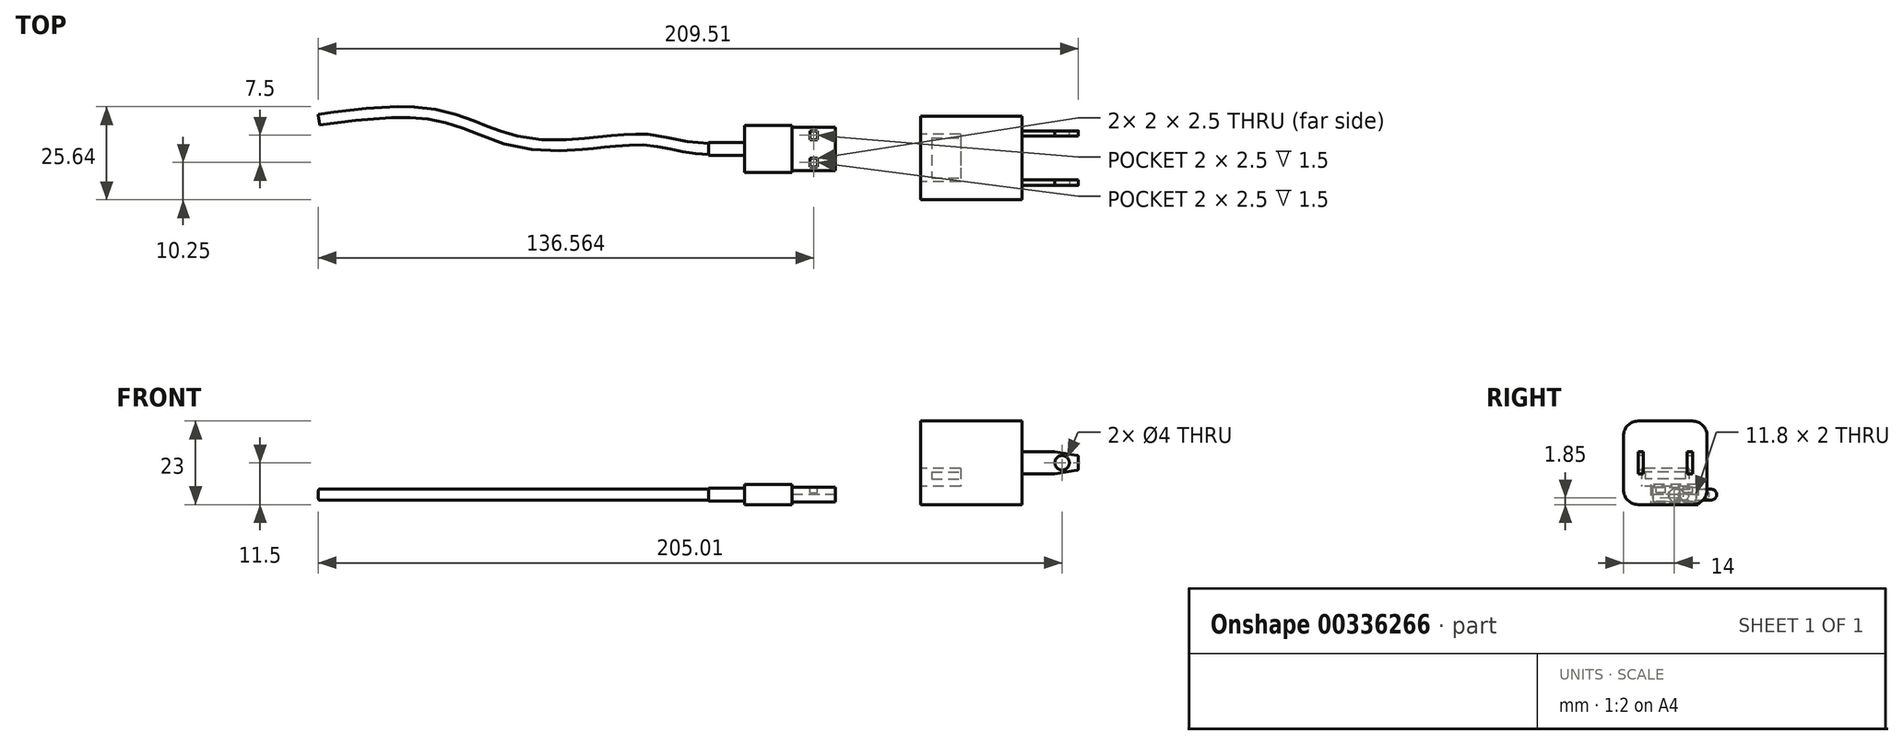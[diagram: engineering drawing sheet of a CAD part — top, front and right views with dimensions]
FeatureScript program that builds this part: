
annotation { "Feature Type Name" : "Feature", "Feature Type Description" : "" }
export const myFeature = defineFeature(function(context is Context, id is Id, definition is map)
    precondition{}
    {
        {
            var Q0;
            Q0=qCreatedBy(makeId("Top.planeOp"),FACE);
            var sketch = newSketch(context, id + "F0", { "sketchPlane" : qUnion([Q0])});
            skLineSegment(sketch, "E0.bottom", {"start": v(-14, 11.5) * mm, "end": v(14, 11.5) * mm});
            skLineSegment(sketch, "E0.top", {"start": v(-14, -11.5) * mm, "end": v(14, -11.5) * mm});
            skLineSegment(sketch, "E0.left", {"start": v(-14, 11.5) * mm, "end": v(-14, -11.5) * mm});
            skLineSegment(sketch, "E0.right", {"start": v(14, 11.5) * mm, "end": v(14, -11.5) * mm});
            skLineSegment(sketch, "E1", {"start": v(0, -11.5) * mm, "end": v(0, 0) * mm});
            skLineSegment(sketch, "E2", {"start": v(0, 0) * mm, "end": v(0, 11.5) * mm});
            skLineSegment(sketch, "E3", {"start": v(14, 0) * mm, "end": v(0, 0) * mm});
            skLineSegment(sketch, "E4", {"start": v(0, 0) * mm, "end": v(-14, 0) * mm});
            skLineSegment(sketch, "E5.bottom", {"start": v(-49.45, 8.5) * mm, "end": v(-37.45, 8.5) * mm});
            skLineSegment(sketch, "E5.top", {"start": v(-49.45, -3.5) * mm, "end": v(-37.45, -3.5) * mm});
            skLineSegment(sketch, "E5.left", {"start": v(-49.45, 8.5) * mm, "end": v(-49.45, -3.5) * mm});
            skLineSegment(sketch, "E5.right", {"start": v(-37.45, 8.5) * mm, "end": v(-37.45, -3.5) * mm});
            skLineSegment(sketch, "E6.bottom", {"start": v(-62.45, 9) * mm, "end": v(-49.45, 9) * mm});
            skLineSegment(sketch, "E6.top", {"start": v(-62.45, -4) * mm, "end": v(-49.45, -4) * mm});
            skLineSegment(sketch, "E6.left", {"start": v(-62.45, 9) * mm, "end": v(-62.45, -4) * mm});
            skLineSegment(sketch, "E6.right", {"start": v(-49.45, 9) * mm, "end": v(-49.45, -4) * mm});
            skPoint(sketch, "E7.endSnap0", {"position": v(-49.45, 2.5) * mm});
            skLineSegment(sketch, "E8.bottom", {"start": v(-44.45, 7.5) * mm, "end": v(-42.45, 7.5) * mm});
            skLineSegment(sketch, "E8.top", {"start": v(-44.45, 5) * mm, "end": v(-42.45, 5) * mm});
            skLineSegment(sketch, "E8.left", {"start": v(-44.45, 7.5) * mm, "end": v(-44.45, 5) * mm});
            skLineSegment(sketch, "E8.right", {"start": v(-42.45, 7.5) * mm, "end": v(-42.45, 5) * mm});
            skLineSegment(sketch, "E9.bottom", {"start": v(-44.45, 0) * mm, "end": v(-42.45, 0) * mm});
            skLineSegment(sketch, "E9.top", {"start": v(-44.45, -2.5) * mm, "end": v(-42.45, -2.5) * mm});
            skLineSegment(sketch, "E9.left", {"start": v(-44.45, 0) * mm, "end": v(-44.45, -2.5) * mm});
            skLineSegment(sketch, "E9.right", {"start": v(-42.45, 0) * mm, "end": v(-42.45, -2.5) * mm});
            skLineSegment(sketch, "E10", {"start": v(-44.45, 6.25) * mm, "end": v(-49.45, 6.25) * mm});
            skLineSegment(sketch, "E11", {"start": v(-44.45, -1.25) * mm, "end": v(-49.45, -1.25) * mm});
            skLineSegment(sketch, "E12", {"start": v(-42.45, 6.25) * mm, "end": v(-37.45, 6.25) * mm});
            skLineSegment(sketch, "E13", {"start": v(-42.45, -1.25) * mm, "end": v(-37.45, -1.25) * mm});
            skLineSegment(sketch, "E14", {"start": v(-43.45, 7.5) * mm, "end": v(-43.45, 8.5) * mm});
            skLineSegment(sketch, "E15", {"start": v(-43.45, -3.5) * mm, "end": v(-43.45, -2.5) * mm});
            skSolve(sketch);
        }
        {
            var Q0;
            {var subQ3=sQuery(id+"F0.wireOp",EDGE,"E1");Q0=makeQuery(id+"F0.imprint","IMPRINT",FACE,{"disambiguationData":[TD([[makeQuery(id+"F0.imprint","IMPRINT",EDGE,{"derivedFrom":subQ3}),-1.0]])]});}
            var Q1;
            {var subQ3=sQuery(id+"F0.wireOp",EDGE,"E2");Q1=makeQuery(id+"F0.imprint","IMPRINT",FACE,{"disambiguationData":[TD([[makeQuery(id+"F0.imprint","IMPRINT",EDGE,{"derivedFrom":subQ3}),-1.0]])]});}
            var Q2;
            {var subQ3=sQuery(id+"F0.wireOp",EDGE,"E2");Q2=makeQuery(id+"F0.imprint","IMPRINT",FACE,{"disambiguationData":[TD([[makeQuery(id+"F0.imprint","IMPRINT",EDGE,{"derivedFrom":subQ3}),1.0]])]});}
            var Q3;
            {var subQ3=sQuery(id+"F0.wireOp",EDGE,"E1");Q3=makeQuery(id+"F0.imprint","IMPRINT",FACE,{"disambiguationData":[TD([[makeQuery(id+"F0.imprint","IMPRINT",EDGE,{"derivedFrom":subQ3}),1.0]])]});}
            extrude(context, id + "F1", {"entities" : qUnion([Q0, Q1, Q2, Q3]), "depth" : 23 * mm});
        }
        {
            var Q0;
            Q0=makeQuery(id+"F1.opExtrude","SWEPT_FACE",FACE,{"disambiguationData":[OSD([sQuery(id+"F0.wireOp",EDGE,"E0.left")])]});
            var sketch = newSketch(context, id + "F2", { "sketchPlane" : qUnion([Q0])});
            skLineSegment(sketch, "E16.bottom", {"start": v(-6.5, 10) * mm, "end": v(6.5, 10) * mm});
            skLineSegment(sketch, "E16.top", {"start": v(-6.5, 5) * mm, "end": v(6.5, 5) * mm});
            skLineSegment(sketch, "E16.left", {"start": v(-6.5, 10) * mm, "end": v(-6.5, 5) * mm});
            skLineSegment(sketch, "E16.right", {"start": v(6.5, 10) * mm, "end": v(6.5, 5) * mm});
            skSolve(sketch);
        }
        {
            var Q0;
            Q0=makeQuery(id+"F1.opExtrude","CAP_EDGE",EDGE,{"disambiguationData":[OSD([sQuery(id+"F0.wireOp",EDGE,"E0.bottom")])],"isStart":false});
            var Q1;
            Q1=makeQuery(id+"F1.opExtrude","CAP_EDGE",EDGE,{"disambiguationData":[OSD([sQuery(id+"F0.wireOp",EDGE,"E0.top")])],"isStart":false});
            var Q2;
            Q2=makeQuery(id+"F1.opExtrude","CAP_EDGE",EDGE,{"disambiguationData":[OSD([sQuery(id+"F0.wireOp",EDGE,"E0.top")])],"isStart":true});
            var Q3;
            Q3=makeQuery(id+"F1.opExtrude","CAP_EDGE",EDGE,{"disambiguationData":[OSD([sQuery(id+"F0.wireOp",EDGE,"E0.bottom")])],"isStart":true});
            fillet(context, id + "F3", {"entities" : qUnion([Q0, Q1, Q2, Q3]), "radius" : 4 * mm, "tangentPropagation" : true, "allowEdgeOverflow" : false});
        }
        {
            var Q0;
            Q0=makeQuery(id+"F1.opExtrude","SWEPT_FACE",FACE,{"disambiguationData":[OSD([sQuery(id+"F0.wireOp",EDGE,"E0.right")])]});
            var sketch = newSketch(context, id + "F4", { "sketchPlane" : qUnion([Q0])});
            skLineSegment(sketch, "E17.bottom", {"start": v(-7.5, 14.5) * mm, "end": v(-6, 14.5) * mm});
            skLineSegment(sketch, "E17.top", {"start": v(-7.5, 8.5) * mm, "end": v(-6, 8.5) * mm});
            skLineSegment(sketch, "E17.left", {"start": v(-7.5, 14.5) * mm, "end": v(-7.5, 8.5) * mm});
            skLineSegment(sketch, "E17.right", {"start": v(-6, 14.5) * mm, "end": v(-6, 8.5) * mm});
            skLineSegment(sketch, "E18.bottom", {"start": v(6, 14.5) * mm, "end": v(7.5, 14.5) * mm});
            skLineSegment(sketch, "E18.top", {"start": v(6, 8.5) * mm, "end": v(7.5, 8.5) * mm});
            skLineSegment(sketch, "E18.left", {"start": v(6, 14.5) * mm, "end": v(6, 8.5) * mm});
            skLineSegment(sketch, "E18.right", {"start": v(7.5, 14.5) * mm, "end": v(7.5, 8.5) * mm});
            skLineSegment(sketch, "E19", {"start": v(-6.75, 14.5) * mm, "end": v(-6.75, 23) * mm});
            skLineSegment(sketch, "E20", {"start": v(-6.75, 8.5) * mm, "end": v(-6.75, 0) * mm});
            skLineSegment(sketch, "E21", {"start": v(6.75, 8.5) * mm, "end": v(6.75, 0) * mm});
            skLineSegment(sketch, "E22", {"start": v(6.75, 14.5) * mm, "end": v(6.75, 23) * mm});
            skLineSegment(sketch, "E23", {"start": v(-7.5, 11.5) * mm, "end": v(-11.5, 11.5) * mm});
            skLineSegment(sketch, "E24", {"start": v(7.5, 11.5) * mm, "end": v(11.5, 11.5) * mm});
            skSolve(sketch);
        }
        {
            var Q0;
            {var subQ0=sQuery(id+"F4.wireOp",EDGE,"E17.right");Q0=makeQuery(id+"F4.imprint","IMPRINT",FACE,{"disambiguationData":[TD([[makeQuery(id+"F4.imprint","IMPRINT",EDGE,{"derivedFrom":subQ0}),-1.0]])]});}
            var Q1;
            {var subQ4=sQuery(id+"F4.wireOp",EDGE,"E18.left");Q1=makeQuery(id+"F4.imprint","IMPRINT",FACE,{"disambiguationData":[TD([[makeQuery(id+"F4.imprint","IMPRINT",EDGE,{"derivedFrom":subQ4}),1.0]])]});}
            extrude(context, id + "F5", {"entities" : qUnion([Q0, Q1]), "depth" : 9 * mm});
        }
        {
            var Q0;
            Q0=makeQuery(id+"F5.opExtrude","SWEPT_FACE",FACE,{"disambiguationData":[OSD([sQuery(id+"F4.wireOp",EDGE,"E17.left")])]});
            var sketch = newSketch(context, id + "F6", { "sketchPlane" : qUnion([Q0])});
            skLineSegment(sketch, "E25", {"start": v(29.5, 13.5) * mm, "end": v(29.5, 9.5) * mm});
            skCircle(sketch, "E26", {"center": v(25, 11.5) * mm, "radius": 2 * mm});
            skPoint(sketch, "E27.endSnap0", {"position": v(23, 11.5) * mm});
            skLineSegment(sketch, "E28", {"start": v(23, 14.5) * mm, "end": v(29.5, 13.5) * mm});
            skLineSegment(sketch, "E29", {"start": v(29.5, 9.5) * mm, "end": v(23, 8.5) * mm});
            skSolve(sketch);
        }
        {
            var Q0;
            Q0=makeQuery(id+"F6.imprint","IMPRINT",FACE,{"disambiguationData":[TD([[makeQuery(id+"F6.imprint","IMPRINT",EDGE,{"derivedFrom":sQuery(id+"F6.wireOp",EDGE,"E25")}),-1.0]])]});
            var Q1;
            Q1=makeQuery(id+"F6.imprint","IMPRINT",FACE,{"disambiguationData":[TD([[makeQuery(id+"F6.imprint","IMPRINT",EDGE,{"derivedFrom":sQuery(id+"F6.wireOp",EDGE,"E26")}),1.0]])]});
            extrude(context, id + "F7", {"entities" : qUnion([Q0, Q1]), "operationType" : NewBodyOperationType.ADD, "oppositeDirection" : true, "depth" : 1.5 * mm});
        }
        {
            var Q0;
            Q0=makeQuery(id+"F6.imprint","IMPRINT",FACE,{"disambiguationData":[TD([[makeQuery(id+"F6.imprint","IMPRINT",EDGE,{"derivedFrom":sQuery(id+"F6.wireOp",EDGE,"E26")}),1.0]])]});
            extrude(context, id + "F8", {"entities" : qUnion([Q0]), "operationType" : NewBodyOperationType.REMOVE, "oppositeDirection" : true, "depth" : 1.5 * mm});
        }
        {
            var Q0;
            Q0=makeQuery(id+"F5.opExtrude","SWEPT_BODY",BODY,{"disambiguationData":[OSD([sQuery(id+"F4.wireOp",EDGE,"E17.bottom"),sQuery(id+"F4.wireOp",EDGE,"E17.top"),sQuery(id+"F4.wireOp",EDGE,"E17.left"),sQuery(id+"F4.wireOp",EDGE,"E17.right")])]});
            var Q1;
            Q1=qCreatedBy(makeId("Front.planeOp"),FACE);
            mirror(context, id + "F9", {"entities" : qUnion([Q0]), "mirrorPlane" : qUnion([Q1])});
        }
        {
            var Q0;
            Q0=makeQuery(id+"F5.opExtrude","SWEPT_BODY",BODY,{"disambiguationData":[OSD([sQuery(id+"F4.wireOp",EDGE,"E18.bottom"),sQuery(id+"F4.wireOp",EDGE,"E18.top"),sQuery(id+"F4.wireOp",EDGE,"E18.left"),sQuery(id+"F4.wireOp",EDGE,"E18.right")])]});
            deleteBodies(context, id + "F10", {"entities" : qUnion([Q0])});
        }
        {
            var Q0;
            Q0=makeQuery(id+"F7.opExtrude","SWEPT_EDGE",EDGE,{"disambiguationData":[OSD([sQuery(id+"F6.wireOp",EDGE,"E25"),sQuery(id+"F6.wireOp",EDGE,"E28")])]});
            var Q1;
            Q1=makeQuery(id+"F7.opExtrude","SWEPT_EDGE",EDGE,{"disambiguationData":[OSD([sQuery(id+"F6.wireOp",EDGE,"E25"),sQuery(id+"F6.wireOp",EDGE,"E29")])]});
            var Q2;
            Q2=makeQuery(id+"F9.opPattern","COPY",EDGE,{"derivedFrom":makeQuery(id+"F7.opExtrude","SWEPT_EDGE",EDGE,{"disambiguationData":[OSD([sQuery(id+"F6.wireOp",EDGE,"E25"),sQuery(id+"F6.wireOp",EDGE,"E28")])]}),"instanceName":"1"});
            var Q3;
            Q3=makeQuery(id+"F9.opPattern","COPY",EDGE,{"derivedFrom":makeQuery(id+"F7.opExtrude","SWEPT_EDGE",EDGE,{"disambiguationData":[OSD([sQuery(id+"F6.wireOp",EDGE,"E25"),sQuery(id+"F6.wireOp",EDGE,"E29")])]}),"instanceName":"1"});
            fillet(context, id + "F11", {"entities" : qUnion([Q0, Q1, Q2, Q3]), "radius" : 0.5 * mm, "tangentPropagation" : true, "allowEdgeOverflow" : false});
        }
        {
            var Q0;
            Q0=makeQuery(id+"F2.imprint","IMPRINT",FACE,{"disambiguationData":[TD([[makeQuery(id+"F2.imprint","IMPRINT",EDGE,{"derivedFrom":sQuery(id+"F2.wireOp",EDGE,"E16.bottom")}),-1.0]])]});
            extrude(context, id + "F12", {"entities" : qUnion([Q0]), "operationType" : NewBodyOperationType.REMOVE, "oppositeDirection" : true, "depth" : 11 * mm});
        }
        {
            var Q0;
            Q0=makeQuery(id+"F12.boolean.opBoolean","COPY",FACE,{"derivedFrom":makeQuery(id+"F12.opExtrude","CAP_FACE",FACE,{"disambiguationData":[OSD([sQuery(id+"F2.wireOp",EDGE,"E16.bottom"),sQuery(id+"F2.wireOp",EDGE,"E16.top"),sQuery(id+"F2.wireOp",EDGE,"E16.left"),sQuery(id+"F2.wireOp",EDGE,"E16.right")])],"isStart":false})});
            var sketch = newSketch(context, id + "F13", { "sketchPlane" : qUnion([Q0])});
            skLineSegment(sketch, "E30.bottom", {"start": v(-5.5, 9) * mm, "end": v(5.5, 9) * mm});
            skLineSegment(sketch, "E30.top", {"start": v(-5.5, 7) * mm, "end": v(5.5, 7) * mm});
            skLineSegment(sketch, "E30.left", {"start": v(-5.5, 9) * mm, "end": v(-5.5, 7) * mm});
            skLineSegment(sketch, "E30.right", {"start": v(5.5, 9) * mm, "end": v(5.5, 7) * mm});
            skSolve(sketch);
        }
        {
            var Q0;
            Q0=makeQuery(id+"F13.imprint","IMPRINT",FACE,{"disambiguationData":[TD([[makeQuery(id+"F13.imprint","IMPRINT",EDGE,{"derivedFrom":sQuery(id+"F13.wireOp",EDGE,"E30.bottom")}),-1.0]])]});
            extrude(context, id + "F14", {"entities" : qUnion([Q0]), "depth" : 8 * mm});
        }
        {
            var Q0;
            {var subQ2=sQuery(id+"F0.wireOp",EDGE,"E6.bottom");Q0=makeQuery(id+"F0.imprint","IMPRINT",FACE,{"disambiguationData":[TD([[makeQuery(id+"F0.imprint","IMPRINT",EDGE,{"derivedFrom":subQ2}),-1.0]])]});}
            extrude(context, id + "F15", {"entities" : qUnion([Q0]), "depth" : 5.5 * mm});
        }
        {
            var Q0;
            Q0=makeQuery(id+"F15.opExtrude","SWEPT_FACE",FACE,{"disambiguationData":[OSD([sQuery(id+"F0.wireOp",EDGE,"E6.right")])]});
            var sketch = newSketch(context, id + "F16", { "sketchPlane" : qUnion([Q0])});
            skLineSegment(sketch, "E31.bottom", {"start": v(-3.5, 4.75) * mm, "end": v(8.5, 4.75) * mm});
            skLineSegment(sketch, "E31.top", {"start": v(-3.5, 0.75) * mm, "end": v(8.5, 0.75) * mm});
            skLineSegment(sketch, "E31.left", {"start": v(-3.5, 4.75) * mm, "end": v(-3.5, 0.75) * mm});
            skLineSegment(sketch, "E31.right", {"start": v(8.5, 4.75) * mm, "end": v(8.5, 0.75) * mm});
            skLineSegment(sketch, "E32", {"start": v(-3.5, 2.75) * mm, "end": v(-4, 2.75) * mm});
            skPoint(sketch, "E32.endSnap0", {"position": v(-4, 2.75) * mm});
            skLineSegment(sketch, "E33", {"start": v(2.5, 4.75) * mm, "end": v(2.5, 5.5) * mm});
            skLineSegment(sketch, "E34", {"start": v(8.5, 2.75) * mm, "end": v(9, 2.75) * mm});
            skLineSegment(sketch, "E35", {"start": v(2.5, 0.75) * mm, "end": v(2.5, 0) * mm});
            skSolve(sketch);
        }
        {
            var Q0;
            {var subQ4=sQuery(id+"F16.wireOp",EDGE,"E31.left");var subQ6=sQuery(id+"F16.wireOp",EDGE,"E31.bottom");var subQ9=makeQuery(id+"F16.imprint","INTERSECT",VERTEX,{"derivedFrom":[subQ6,subQ4]});Q0=makeQuery(id+"F16.imprint","IMPRINT",FACE,{"disambiguationData":[TD([[makeQuery(id+"F16.imprint","IMPRINT",EDGE,{"disambiguationData":[TD([[subQ9,-1.0]])],"derivedFrom":subQ6}),-1.0]])]});}
            extrude(context, id + "F17", {"entities" : qUnion([Q0]), "depth" : 12 * mm});
        }
        {
            var Q0;
            Q0=makeQuery(id+"F17.opExtrude","CAP_FACE",FACE,{"disambiguationData":[OSD([sQuery(id+"F16.wireOp",EDGE,"E31.bottom"),sQuery(id+"F16.wireOp",EDGE,"E31.top"),sQuery(id+"F16.wireOp",EDGE,"E31.left"),sQuery(id+"F16.wireOp",EDGE,"E31.right")])],"isStart":false});
            var sketch = newSketch(context, id + "F18", { "sketchPlane" : qUnion([Q0])});
            skLineSegment(sketch, "E36.bottom", {"start": v(-3.4, 2.85) * mm, "end": v(8.4, 2.85) * mm});
            skLineSegment(sketch, "E36.top", {"start": v(-3.4, 0.85) * mm, "end": v(8.4, 0.85) * mm});
            skLineSegment(sketch, "E36.left", {"start": v(-3.4, 2.85) * mm, "end": v(-3.4, 0.85) * mm});
            skLineSegment(sketch, "E36.right", {"start": v(8.4, 2.85) * mm, "end": v(8.4, 0.85) * mm});
            skLineSegment(sketch, "E37", {"start": v(-3.4, 1.85) * mm, "end": v(-3.5, 1.85) * mm});
            skSolve(sketch);
        }
        {
            var Q0;
            {var subQ3=sQuery(id+"F18.wireOp",EDGE,"E36.bottom");Q0=makeQuery(id+"F18.imprint","IMPRINT",FACE,{"disambiguationData":[TD([[makeQuery(id+"F18.imprint","IMPRINT",EDGE,{"derivedFrom":subQ3}),-1.0]])]});}
            extrude(context, id + "F19", {"entities" : qUnion([Q0]), "operationType" : NewBodyOperationType.REMOVE, "oppositeDirection" : true, "depth" : 12 * mm});
        }
        {
            var Q0;
            Q0=makeQuery(id+"F17.opExtrude","SWEPT_FACE",FACE,{"disambiguationData":[OSD([sQuery(id+"F16.wireOp",EDGE,"E31.bottom")])]});
            var sketch = newSketch(context, id + "F20", { "sketchPlane" : qUnion([Q0])});
            skLineSegment(sketch, "E38.bottom", {"start": v(-44.45, 7.5) * mm, "end": v(-42.45, 7.5) * mm});
            skLineSegment(sketch, "E38.top", {"start": v(-44.45, 5) * mm, "end": v(-42.45, 5) * mm});
            skLineSegment(sketch, "E38.left", {"start": v(-44.45, 7.5) * mm, "end": v(-44.45, 5) * mm});
            skLineSegment(sketch, "E38.right", {"start": v(-42.45, 7.5) * mm, "end": v(-42.45, 5) * mm});
            skLineSegment(sketch, "E39.bottom", {"start": v(-44.45, 0) * mm, "end": v(-42.45, 0) * mm});
            skLineSegment(sketch, "E39.top", {"start": v(-44.45, -2.5) * mm, "end": v(-42.45, -2.5) * mm});
            skLineSegment(sketch, "E39.left", {"start": v(-44.45, 0) * mm, "end": v(-44.45, -2.5) * mm});
            skLineSegment(sketch, "E39.right", {"start": v(-42.45, 0) * mm, "end": v(-42.45, -2.5) * mm});
            skSolve(sketch);
        }
        {
            var Q0;
            Q0=makeQuery(id+"F20.imprint","IMPRINT",FACE,{"disambiguationData":[TD([[makeQuery(id+"F20.imprint","IMPRINT",EDGE,{"derivedFrom":sQuery(id+"F20.wireOp",EDGE,"E38.bottom")}),-1.0]])]});
            extrude(context, id + "F21", {"entities" : qUnion([Q0]), "operationType" : NewBodyOperationType.REMOVE, "oppositeDirection" : true, "depth" : 1.5 * mm});
        }
        {
            var Q0;
            Q0=makeQuery(id+"F20.imprint","IMPRINT",FACE,{"disambiguationData":[TD([[makeQuery(id+"F20.imprint","IMPRINT",EDGE,{"derivedFrom":sQuery(id+"F20.wireOp",EDGE,"E39.bottom")}),-1.0]])]});
            extrude(context, id + "F22", {"entities" : qUnion([Q0]), "operationType" : NewBodyOperationType.REMOVE, "oppositeDirection" : true, "depth" : 1.5 * mm});
        }
        {
            var Q0;
            {var subQ1=sQuery(id+"F0.wireOp",EDGE,"E9.bottom");Q0=makeQuery(id+"F0.imprint","IMPRINT",FACE,{"disambiguationData":[TD([[makeQuery(id+"F0.imprint","IMPRINT",EDGE,{"derivedFrom":subQ1}),-1.0]])]});}
            extrude(context, id + "F23", {"entities" : qUnion([Q0]), "operationType" : NewBodyOperationType.REMOVE, "depth" : 2 * mm});
        }
        {
            var Q0;
            {var subQ4=sQuery(id+"F0.wireOp",EDGE,"E8.top");Q0=makeQuery(id+"F0.imprint","IMPRINT",FACE,{"disambiguationData":[TD([[makeQuery(id+"F0.imprint","IMPRINT",EDGE,{"derivedFrom":subQ4}),1.0]])]});}
            extrude(context, id + "F24", {"entities" : qUnion([Q0]), "operationType" : NewBodyOperationType.REMOVE, "depth" : 2 * mm});
        }
        {
            var Q0;
            Q0=makeQuery(id+"F15.opExtrude","SWEPT_FACE",FACE,{"disambiguationData":[OSD([sQuery(id+"F0.wireOp",EDGE,"E6.left")])]});
            var sketch = newSketch(context, id + "F25", { "sketchPlane" : qUnion([Q0])});
            skCircle(sketch, "E40", {"center": v(-2.5, 2.75) * mm, "radius": 1.75 * mm});
            skPoint(sketch, "E40.centerSnap0", {"position": v(4, 2.75) * mm});
            skLineSegment(sketch, "E41", {"start": v(-2.5, 2.75) * mm, "end": v(-9, 2.75) * mm});
            skLineSegment(sketch, "E42", {"start": v(-2.5, 2.75) * mm, "end": v(4, 2.75) * mm});
            skLineSegment(sketch, "E43", {"start": v(-2.5, 2.75) * mm, "end": v(-2.5, 5.5) * mm});
            skLineSegment(sketch, "E44", {"start": v(-2.5, 2.75) * mm, "end": v(-2.5, 0) * mm});
            skSolve(sketch);
        }
        {
            var Q0;
            {var subQ0=sQuery(id+"F25.wireOp",EDGE,"E43");var subQ1=sQuery(id+"F25.wireOp",EDGE,"E40");var subQ2=makeQuery(id+"F25.imprint","INTERSECT",VERTEX,{"derivedFrom":[subQ1,subQ0]});Q0=makeQuery(id+"F25.imprint","IMPRINT",FACE,{"disambiguationData":[TD([[makeQuery(id+"F25.imprint","IMPRINT",EDGE,{"disambiguationData":[TD([[subQ2,-1.0]])],"derivedFrom":subQ1}),1.0]])]});}
            var Q1;
            {var subQ0=sQuery(id+"F25.wireOp",EDGE,"E43");var subQ1=sQuery(id+"F25.wireOp",EDGE,"E40");var subQ2=makeQuery(id+"F25.imprint","INTERSECT",VERTEX,{"derivedFrom":[subQ1,subQ0]});Q1=makeQuery(id+"F25.imprint","IMPRINT",FACE,{"disambiguationData":[TD([[makeQuery(id+"F25.imprint","IMPRINT",EDGE,{"disambiguationData":[TD([[subQ2,1.0]])],"derivedFrom":subQ1}),1.0]])]});}
            var Q2;
            {var subQ0=sQuery(id+"F25.wireOp",EDGE,"E42");var subQ1=sQuery(id+"F25.wireOp",EDGE,"E40");var subQ2=makeQuery(id+"F25.imprint","INTERSECT",VERTEX,{"derivedFrom":[subQ1,subQ0]});Q2=makeQuery(id+"F25.imprint","IMPRINT",FACE,{"disambiguationData":[TD([[makeQuery(id+"F25.imprint","IMPRINT",EDGE,{"disambiguationData":[TD([[subQ2,1.0]])],"derivedFrom":subQ1}),1.0]])]});}
            var Q3;
            {var subQ0=sQuery(id+"F25.wireOp",EDGE,"E41");var subQ1=sQuery(id+"F25.wireOp",EDGE,"E40");var subQ2=makeQuery(id+"F25.imprint","INTERSECT",VERTEX,{"derivedFrom":[subQ1,subQ0]});Q3=makeQuery(id+"F25.imprint","IMPRINT",FACE,{"disambiguationData":[TD([[makeQuery(id+"F25.imprint","IMPRINT",EDGE,{"disambiguationData":[TD([[subQ2,-1.0]])],"derivedFrom":subQ1}),1.0]])]});}
            extrude(context, id + "F26", {"entities" : qUnion([Q0, Q1, Q2, Q3]), "depth" : 10 * mm});
        }
        {
            var Q0;
            Q0=makeQuery(id+"F26.opExtrude","CAP_FACE",FACE,{"disambiguationData":[OSD([sQuery(id+"F25.wireOp",EDGE,"E40")])],"isStart":false});
            var sketch = newSketch(context, id + "F27", { "sketchPlane" : qUnion([Q0])});
            skCircle(sketch, "E45", {"center": v(-2.5, 2.75) * mm, "radius": 1.5 * mm});
            skSolve(sketch);
        }
        {
            var Q0;
            Q0=qCreatedBy(makeId("Top.planeOp"),FACE);
            cPlane(context, id + "F28", {"entities" : qUnion([Q0]), "cplaneType" : CPlaneType.OFFSET, "offset" : 2.75 * mm, "width" : 150 * mm, "height" : 150 * mm});
        }
        {
            var Q0;
            Q0=qCreatedBy(id+"F28.planeOp",FACE);
            var sketch = newSketch(context, id + "F29", { "sketchPlane" : qUnion([Q0])});
            skFitSpline(sketch, "E46", {"points": [v(-72.45, 2.5) * mm, v(-88.89, 4.99) * mm, v(-109.68, 3.67) * mm, v(-128.02, 5.24) * mm, v(-147.85, 11.92) * mm, v(-179.78, 10.54) * mm], "startDerivative": vector(-126.5, 3.04) * mm, "endDerivative": vector(-139.1, -18.25) * mm});
            skSolve(sketch);
        }
        {
            var Q0;
            Q0=makeQuery(id+"F27.imprint","IMPRINT",FACE,{"disambiguationData":[TD([[makeQuery(id+"F27.imprint","IMPRINT",EDGE,{"derivedFrom":sQuery(id+"F27.wireOp",EDGE,"E45")}),1.0]])]});
            var Q1;
            Q1=sQuery(id+"F29.wireOp",EDGE,"E46");
            sweep(context, id + "F30", {"operationType" : NewBodyOperationType.ADD, "profiles" : qUnion([Q0]), "path" : qUnion([Q1])});
        }
    });
